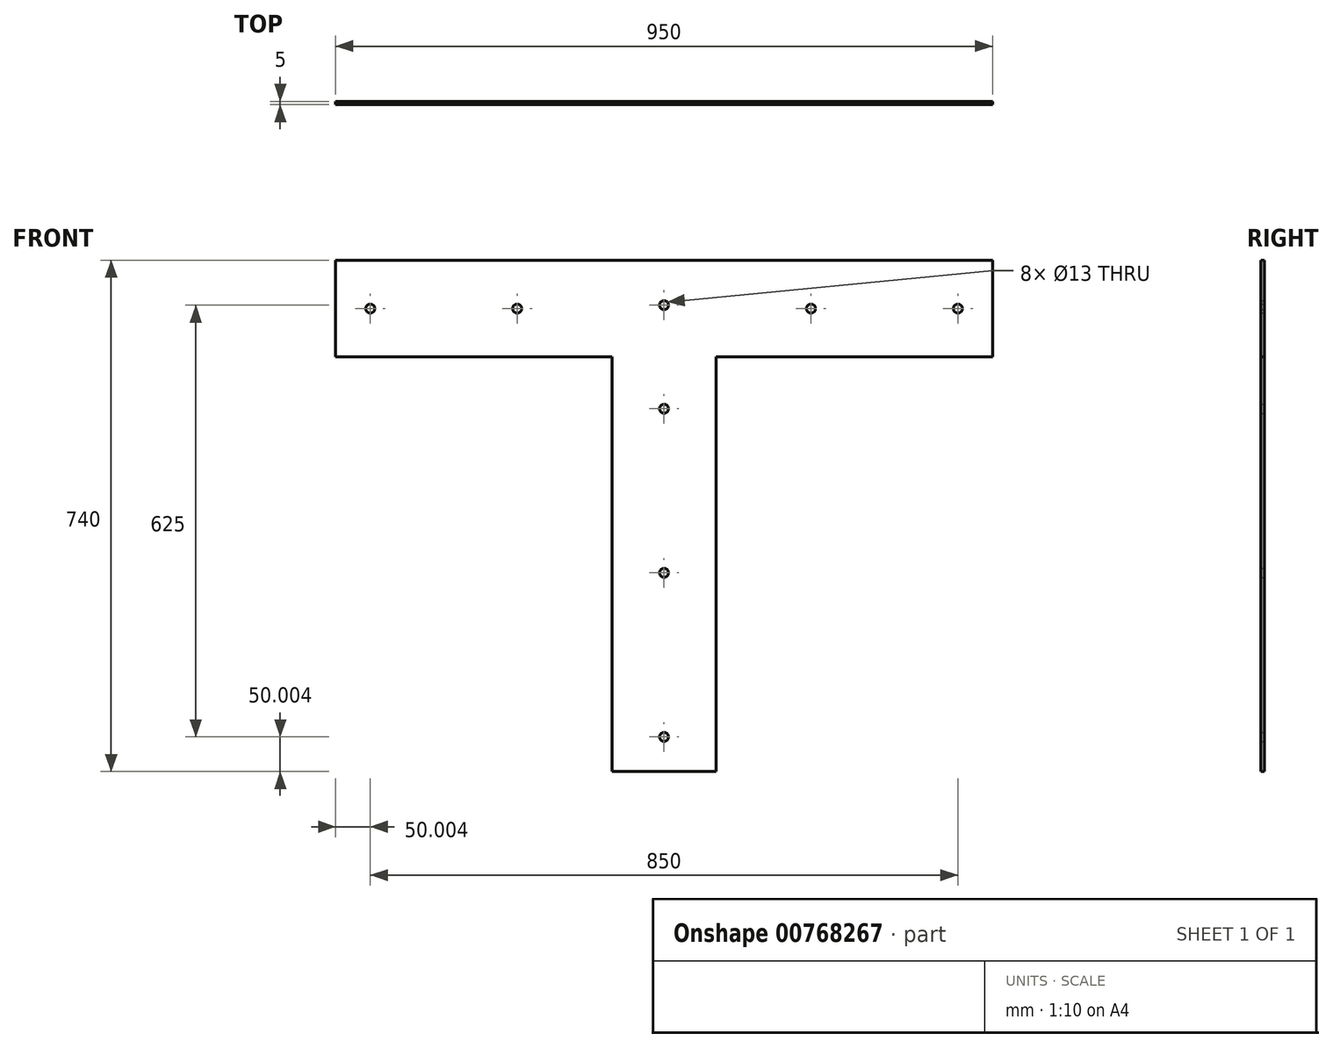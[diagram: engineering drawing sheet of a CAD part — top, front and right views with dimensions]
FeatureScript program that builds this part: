
annotation { "Feature Type Name" : "Feature", "Feature Type Description" : "" }
export const myFeature = defineFeature(function(context is Context, id is Id, definition is map)
    precondition{}
    {
        {
            var Q0;
            Q0=qCreatedBy(makeId("Front.planeOp"),FACE);
            var sketch = newSketch(context, id + "F0", { "sketchPlane" : qUnion([Q0])});
            skLineSegment(sketch, "E0", {"start": v(-321.05, -443.09) * mm, "end": v(-321.05, 156.91) * mm});
            skLineSegment(sketch, "E1", {"start": v(228.95, 296.91) * mm, "end": v(228.95, 156.91) * mm});
            skLineSegment(sketch, "E2", {"start": v(228.95, 156.91) * mm, "end": v(-171.05, 156.91) * mm});
            skLineSegment(sketch, "E3", {"start": v(-171.05, 156.91) * mm, "end": v(-171.05, -443.09) * mm});
            skLineSegment(sketch, "E4", {"start": v(-171.05, -443.09) * mm, "end": v(-321.05, -443.09) * mm});
            skCircle(sketch, "E5", {"center": v(178.95, 226.91) * mm, "radius": 6.5 * mm});
            skCircle(sketch, "E6", {"center": v(-33.55, 226.91) * mm, "radius": 6.5 * mm});
            skCircle(sketch, "E7", {"center": v(-246.05, 231.91) * mm, "radius": 6.5 * mm});
            skCircle(sketch, "E8", {"center": v(-246.05, -393.09) * mm, "radius": 6.5 * mm});
            skPoint(sketch, "E8.centerSnap0", {"position": v(-246.05, -443.09) * mm});
            skCircle(sketch, "E9", {"center": v(-246.05, 81.91) * mm, "radius": 6.5 * mm});
            skCircle(sketch, "E10", {"center": v(-246.05, -155.59) * mm, "radius": 6.5 * mm});
            skLineSegment(sketch, "E11.MirrorCS", {"start": v(-721.05, 296.91) * mm, "end": v(-721.05, 156.91) * mm});
            skCircle(sketch, "E12.MirrorC", {"center": v(-458.55, 226.91) * mm, "radius": 6.5 * mm});
            skCircle(sketch, "E13.MirrorC", {"center": v(-671.05, 226.91) * mm, "radius": 6.5 * mm});
            skLineSegment(sketch, "E14", {"start": v(228.95, 296.91) * mm, "end": v(-721.05, 296.91) * mm});
            skLineSegment(sketch, "E15", {"start": v(-721.05, 156.91) * mm, "end": v(-321.05, 156.91) * mm});
            skSolve(sketch);
        }
        {
            var Q0;
            Q0=makeQuery(id+"F0.imprint","IMPRINT",FACE,{"disambiguationData":[TD([[makeQuery(id+"F0.imprint","IMPRINT",EDGE,{"derivedFrom":sQuery(id+"F0.wireOp",EDGE,"E0")}),-1.0]])]});
            extrude(context, id + "F1", {"entities" : qUnion([Q0]), "depth" : 5 * mm, "offsetDistance" : 25 * mm});
        }
    });
